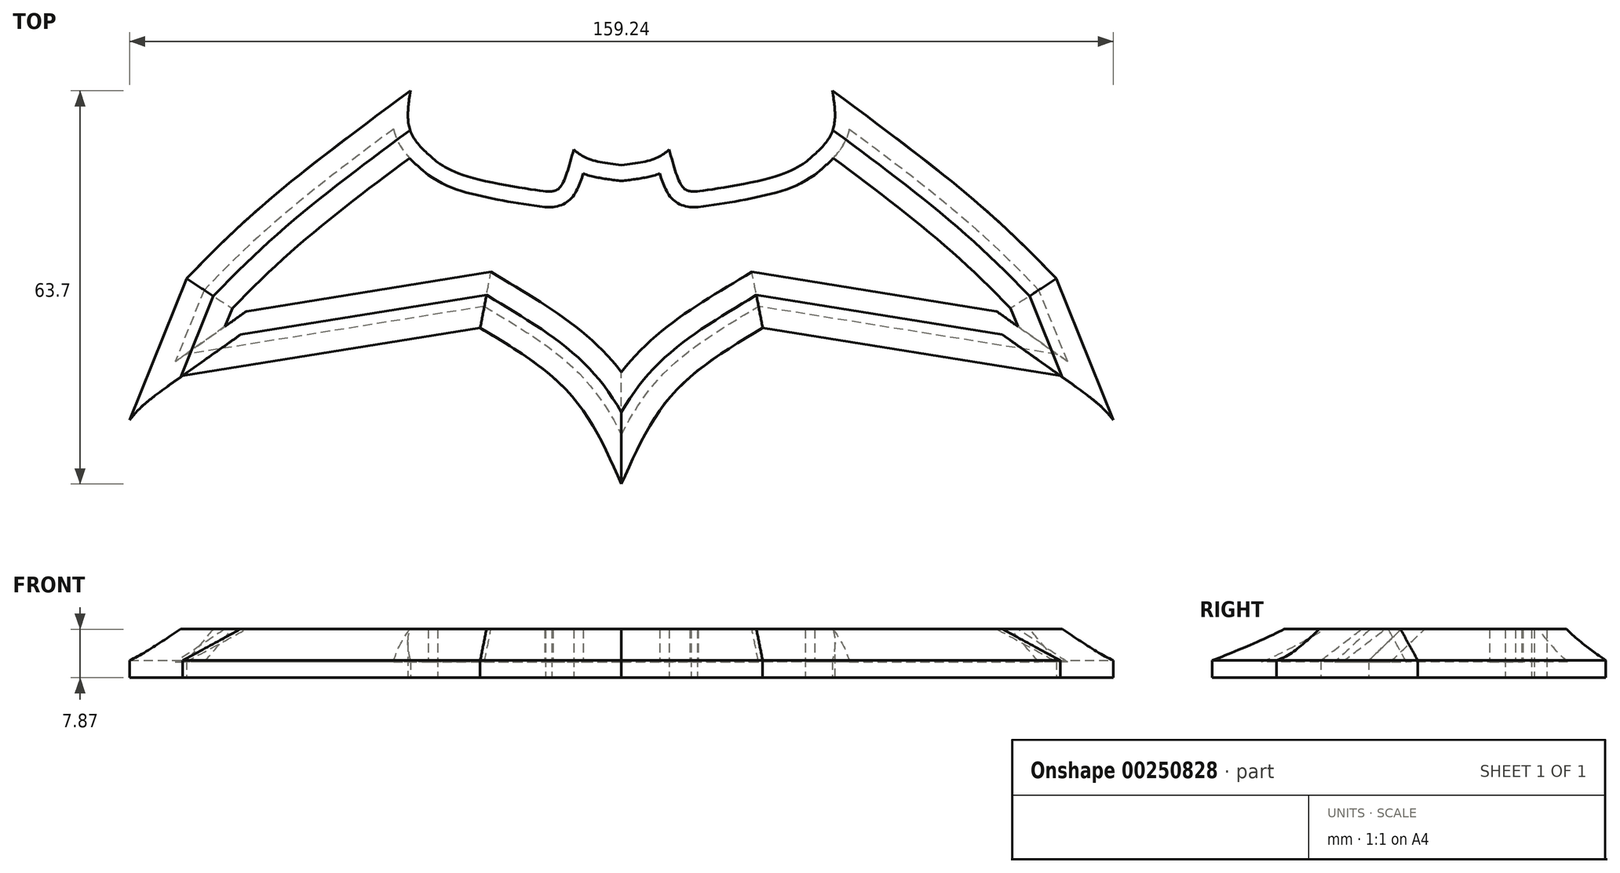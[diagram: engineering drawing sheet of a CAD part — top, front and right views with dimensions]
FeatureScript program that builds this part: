
annotation { "Feature Type Name" : "Feature", "Feature Type Description" : "" }
export const myFeature = defineFeature(function(context is Context, id is Id, definition is map)
    precondition{}
    {
        {
            var Q0;
            Q0=qCreatedBy(makeId("Top.planeOp"),FACE);
            var sketch = newSketch(context, id + "F0", { "sketchPlane" : qUnion([Q0])});
            skFitSpline(sketch, "E0", {"points": [v(-79.62, -33.82) * mm, v(-77.4, -31.47) * mm, v(-71.05, -26.68) * mm], "startDerivative": vector(4.79, 5.69) * mm, "endDerivative": vector(11.84, 8.39) * mm});
            skPoint(sketch, "E1.2.internal.orphan", {"position": v(0, -44.46) * mm});
            skPoint(sketch, "E1.3.internal.orphan", {"position": v(0, -44.23) * mm});
            skLineSegment(sketch, "E2", {"start": v(-71.05, -26.68) * mm, "end": v(-22.86, -18.93) * mm});
            skFitSpline(sketch, "E3", {"points": [v(-22.86, -18.93) * mm, v(-8.22, -29.73) * mm, v(0, -44.23) * mm], "startDerivative": vector(31.68, -18.96) * mm, "endDerivative": vector(13.9, -31.72) * mm});
            skFitSpline(sketch, "E4", {"points": [v(-75.42, -16.3) * mm, v(-59.1, 0) * mm, v(-34.14, 19.47) * mm], "startDerivative": vector(32.95, 35.21) * mm, "endDerivative": vector(49.19, 36.28) * mm});
            skPoint(sketch, "E5.1.internal.orphan", {"position": v(-34.14, 12.9) * mm});
            skFitSpline(sketch, "E6", {"points": [v(-34.14, 19.47) * mm, v(-34.14, 12.9) * mm, v(-29.75, 7.87) * mm], "startDerivative": vector(-2.18, -13.97) * mm, "endDerivative": vector(10.94, -9.23) * mm});
            skFitSpline(sketch, "E7", {"points": [v(-29.75, 7.87) * mm, v(-24.71, 5.54) * mm, v(-12.3, 3.2) * mm, v(-11.95, 3.2) * mm], "startDerivative": vector(10.05, -6.54) * mm, "endDerivative": vector(2.12, 0.3) * mm});
            skFitSpline(sketch, "E8", {"points": [v(-11.95, 3.2) * mm, v(-11.33, 3.2) * mm, v(-11.27, 3.2) * mm], "startDerivative": vector(1.02, 0) * mm, "endDerivative": vector(0.19, 0) * mm});
            skFitSpline(sketch, "E9", {"points": [v(-11.27, 3.2) * mm, v(-10.01, 3.76) * mm, v(-7.73, 9.94) * mm], "startDerivative": vector(4.12, 0.65) * mm, "endDerivative": vector(3.09, 11.49) * mm});
            skFitSpline(sketch, "E10", {"points": [v(-7.73, 9.94) * mm, v(-5.45, 8.5) * mm, v(0, 7.42) * mm], "startDerivative": vector(4.8, -3.85) * mm, "endDerivative": vector(10.34, -1.34) * mm});
            skLineSegment(sketch, "E11", {"start": v(-12.3, 3.2) * mm, "end": v(-11.27, 3.2) * mm});
            skLineSegment(sketch, "E12", {"start": v(-12.3, 3.2) * mm, "end": v(-11.33, 3.2) * mm});
            skPoint(sketch, "E13.MirrorCS.0.internal.orphan", {"position": v(11.27, 3.2) * mm});
            skPoint(sketch, "E13.MirrorCS.end.orphan", {"position": v(7.73, 9.94) * mm});
            skPoint(sketch, "E14.MirrorCS.start.orphan", {"position": v(29.75, 7.87) * mm});
            skPoint(sketch, "E15.MirrorCS.end.orphan", {"position": v(12.3, 3.2) * mm});
            skPoint(sketch, "E16.MirrorCS.start.orphan", {"position": v(34.14, 19.47) * mm});
            skPoint(sketch, "E17.MirrorCS.start.orphan", {"position": v(70.38, -10.94) * mm});
            skPoint(sketch, "E18.MirrorCS.2.internal.orphan", {"position": v(71.05, -26.68) * mm});
            skPoint(sketch, "E18.MirrorCS.start.orphan", {"position": v(79.62, -33.82) * mm});
            skPoint(sketch, "E19.MirrorCS.end.orphan", {"position": v(22.86, -18.93) * mm});
            skPoint(sketch, "E20.orphan", {"position": v(11.95, 3.2) * mm});
            skFitSpline(sketch, "E21.MirrorCS", {"points": [v(7.73, 9.94) * mm, v(5.45, 8.5) * mm, v(0, 7.42) * mm], "startDerivative": vector(-4.8, -3.85) * mm, "endDerivative": vector(-10.34, -1.34) * mm});
            skFitSpline(sketch, "E22.MirrorCS", {"points": [v(11.27, 3.2) * mm, v(10.01, 3.76) * mm, v(7.73, 9.94) * mm], "startDerivative": vector(-4.12, 0.65) * mm, "endDerivative": vector(-3.09, 11.49) * mm});
            skFitSpline(sketch, "E23.MirrorCS", {"points": [v(29.75, 7.87) * mm, v(24.71, 5.54) * mm, v(12.3, 3.2) * mm, v(11.95, 3.2) * mm], "startDerivative": vector(-10.05, -6.54) * mm, "endDerivative": vector(-2.12, 0.3) * mm});
            skLineSegment(sketch, "E24.MirrorCS", {"start": v(12.3, 3.2) * mm, "end": v(11.27, 3.2) * mm});
            skFitSpline(sketch, "E25.MirrorCS", {"points": [v(34.14, 19.47) * mm, v(34.14, 12.9) * mm, v(29.75, 7.87) * mm], "startDerivative": vector(2.18, -13.97) * mm, "endDerivative": vector(-10.94, -9.23) * mm});
            skFitSpline(sketch, "E26.MirrorCS", {"points": [v(75.42, -16.3) * mm, v(59.1, 0) * mm, v(34.14, 19.47) * mm], "startDerivative": vector(-32.95, 35.21) * mm, "endDerivative": vector(-49.19, 36.28) * mm});
            skFitSpline(sketch, "E27.MirrorCS", {"points": [v(79.62, -33.82) * mm, v(77.4, -31.47) * mm, v(71.05, -26.68) * mm], "startDerivative": vector(-4.79, 5.69) * mm, "endDerivative": vector(-11.84, 8.39) * mm});
            skLineSegment(sketch, "E28.MirrorCS", {"start": v(71.05, -26.68) * mm, "end": v(22.86, -18.93) * mm});
            skFitSpline(sketch, "E29.MirrorCS", {"points": [v(22.86, -18.93) * mm, v(8.22, -29.73) * mm, v(0, -44.23) * mm], "startDerivative": vector(-31.68, -18.96) * mm, "endDerivative": vector(-13.9, -31.72) * mm});
            skLineSegment(sketch, "E30", {"start": v(-70.4, -10.98) * mm, "end": v(-79.62, -33.82) * mm});
            skLineSegment(sketch, "E31.MirrorCS", {"start": v(70.4, -10.98) * mm, "end": v(79.62, -33.82) * mm});
            skLineSegment(sketch, "E32", {"start": v(70.38, -10.94) * mm, "end": v(70.4, -10.98) * mm});
            skLineSegment(sketch, "E33.MirrorCS", {"start": v(-70.38, -10.94) * mm, "end": v(-70.4, -10.98) * mm});
            skSolve(sketch);
        }
        {
            var Q0;
            Q0 = qSketchRegion(id + "F0", true);
            extrude(context, id + "F1", {"entities" : qUnion([Q0]), "depth" : 7.87 * mm});
        }
        {
            var Q0;
            Q0=makeQuery(id+"F1.opExtrude","CAP_EDGE",EDGE,{"disambiguationData":[OSD([sQuery(id+"F0.wireOp",EDGE,"E31.MirrorCS")])],"isStart":false});
            var Q1;
            Q1=makeQuery(id+"F1.opExtrude","CAP_EDGE",EDGE,{"disambiguationData":[OSD([sQuery(id+"F0.wireOp",EDGE,"E30")])],"isStart":false});
            var Q2;
            Q2=makeQuery(id+"F1.opExtrude","CAP_EDGE",EDGE,{"disambiguationData":[OSD([sQuery(id+"F0.wireOp",EDGE,"E29.MirrorCS")])],"isStart":false});
            var Q3;
            Q3=makeQuery(id+"F1.opExtrude","CAP_EDGE",EDGE,{"disambiguationData":[OSD([sQuery(id+"F0.wireOp",EDGE,"E3")])],"isStart":false});
            var Q4;
            Q4=makeQuery(id+"F1.opExtrude","CAP_EDGE",EDGE,{"disambiguationData":[OSD([sQuery(id+"F0.wireOp",EDGE,"E4")])],"isStart":false});
            var Q5;
            Q5=makeQuery(id+"F1.opExtrude","CAP_EDGE",EDGE,{"disambiguationData":[OSD([sQuery(id+"F0.wireOp",EDGE,"E26.MirrorCS")])],"isStart":false});
            var Q6;
            Q6=makeQuery(id+"F1.opExtrude","CAP_EDGE",EDGE,{"disambiguationData":[OSD([sQuery(id+"F0.wireOp",EDGE,"E2")])],"isStart":false});
            var Q7;
            Q7=makeQuery(id+"F1.opExtrude","CAP_EDGE",EDGE,{"disambiguationData":[OSD([sQuery(id+"F0.wireOp",EDGE,"E28.MirrorCS")])],"isStart":false});
            chamfer(context, id + "F2", {"entities" : qUnion([Q0, Q1, Q2, Q3, Q4, Q5, Q6, Q7]), "width" : 5.08 * mm, "tangentPropagation" : true});
        }
        {
            var Q0;
            Q0=makeQuery(id+"F1.opExtrude","CAP_FACE",FACE,{"disambiguationData":[OSD([sQuery(id+"F0.wireOp",EDGE,"E0"),sQuery(id+"F0.wireOp",EDGE,"E2"),sQuery(id+"F0.wireOp",EDGE,"E3"),sQuery(id+"F0.wireOp",EDGE,"E4"),sQuery(id+"F0.wireOp",EDGE,"E6"),sQuery(id+"F0.wireOp",EDGE,"E7"),sQuery(id+"F0.wireOp",EDGE,"E9"),sQuery(id+"F0.wireOp",EDGE,"E10"),sQuery(id+"F0.wireOp",EDGE,"E11"),sQuery(id+"F0.wireOp",EDGE,"E12"),sQuery(id+"F0.wireOp",EDGE,"E21.MirrorCS"),sQuery(id+"F0.wireOp",EDGE,"E22.MirrorCS"),sQuery(id+"F0.wireOp",EDGE,"E24.MirrorCS"),sQuery(id+"F0.wireOp",EDGE,"E25.MirrorCS"),sQuery(id+"F0.wireOp",EDGE,"E23.MirrorCS"),sQuery(id+"F0.wireOp",EDGE,"E26.MirrorCS"),sQuery(id+"F0.wireOp",EDGE,"E27.MirrorCS"),sQuery(id+"F0.wireOp",EDGE,"E28.MirrorCS"),sQuery(id+"F0.wireOp",EDGE,"E29.MirrorCS"),sQuery(id+"F0.wireOp",EDGE,"E30"),sQuery(id+"F0.wireOp",EDGE,"E31.MirrorCS"),sQuery(id+"F0.wireOp",EDGE,"E32"),sQuery(id+"F0.wireOp",EDGE,"E33.MirrorCS")])],"isStart":false});
            shell(context, id + "F3", {"entities" : qUnion([Q0]), "thickness" : 2.54 * mm});
        }
    });
